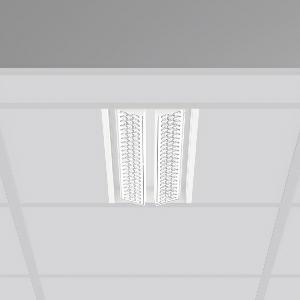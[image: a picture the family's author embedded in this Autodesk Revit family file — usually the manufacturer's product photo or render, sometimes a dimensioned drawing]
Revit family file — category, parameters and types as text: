
# Revit family: tx-move_901736_002_1_b471
name_source: partatom
category: Lighting Fixtures
units: mm (PartAtom-declared; Revit-internal decimal feet)

## family parameters
Cut with Voids When Loaded = No
Host = Face
Light Source = No
Part Type = Normal
Room Calculation Point = No
Round Connector Dimension = Use Diameter
Shared = No

## types (1)
- MultiLumen 1 (1 x LED Modul 840, 2800 lm, 4000)
    Apparent Load = 35 VA
    Approval mark = CE
    CIE Flux Codes = 90 97 99 100 100
    Color Rendering = 80
    Color Temperature = 4000
    Default Elevation = 1800 mm
    Description = Series: TX-MOVE
Einlege/Einbau-Flächenstrahler. Housing: sheet steel, powder-coated. 2xSwivel range: 90°. High-efficiency LED units with optimum light control thanks to clear plastic (PC) lens optics. Spezielle Mikrostrukturen reduzieren Gelbsaum. Symmetrical light distribution. Suitable for laying in grid ceiling module 625. Connected converter included in separate gearbox.Suitable for through-wiring.MultiLumen: Luminous flux adjustable in 3 steps. Accessories: Mounting frame for installation in suspended ceilings. Environmentally friendly and resource-saving due to replaceable and recyclable components. 
Colour: traffic white, matt (RAL 9016)
Length: 622 mm
Width: 190 mm
Height: 39 mm
Cut-out length: 602 mm
Cut-out width: 174 mm
Recess height: 100 mm
Lamp: LED
Socket: without socket
Colour temperature: 4000K
Colour rendering index (CRI): 80
System power: 35 W
Rated luminous flux: 5600 lm
Luminous efficiency: 160 lm/W
System power 2: 47 W
Rated luminous flux 2: 7300 lm
Luminous efficiency 2: 155 lm/W
System power 3: 68 W
Rated luminous flux 3: 10000 lm
Luminous efficiency 3: 147 lm/W
Control gear: Regulated power supply
Protection class: I
Type of protection: IP 20
    Height = 0 mm  [stored 0 ft]
    Lamp = 1 x LED Modul 840
    Lamp Light Flux = 2800 lm
    Lamp count = 1
    Length = 622 mm
    Lifetime = 50000 h
    Luminous efficacy = 160 lm/W
    Manufacturer = RZB
    ModVariant = No
    Model = 901736.002.1
    Mounting Place = Ceiling, Wall
    Mounting Type = Recessed
    Number of Poles = 1
    OnlyDefault = Yes
    Power Factor = 1
    Product Name = TX-MOVE
    Product group = Recessed projectors
    ProductGroupID = 401
    Protection Class = Protection class I
    Protection Degree = IP 20
    RLX_Detail_Level = 1
    RLX_Emergency_Light_Flux = 0 lm
    RLX_Emergency_Type = 0
    RLX_Emergency_Type_DB = No
    RlxData = <blob elided: 34005 chars, md5=b20ae122>
    Socket = socket
    Standby Power = 0 W
    System Light Flux = 5600 lm
    System Power = 35 W
    Type Comments = MultiLumen 1
    Type Image = 901737.002.jpg
    URL = http://relux.com
    VarID = multilumen_1
    Voltage = 230 V
    Voltage Range = 220-240 V
    Weight = 0.00 kg
    Width = 190 mm  [stored 0.62336 ft]

note: [stored X ft] marks values corroborated as IEEE doubles in the binary element streams (Revit-internal decimal feet)

## geometry (parser evidence)
native form markers: Blend x4, Sweep x13
no freeform markers — native parametric forms only
